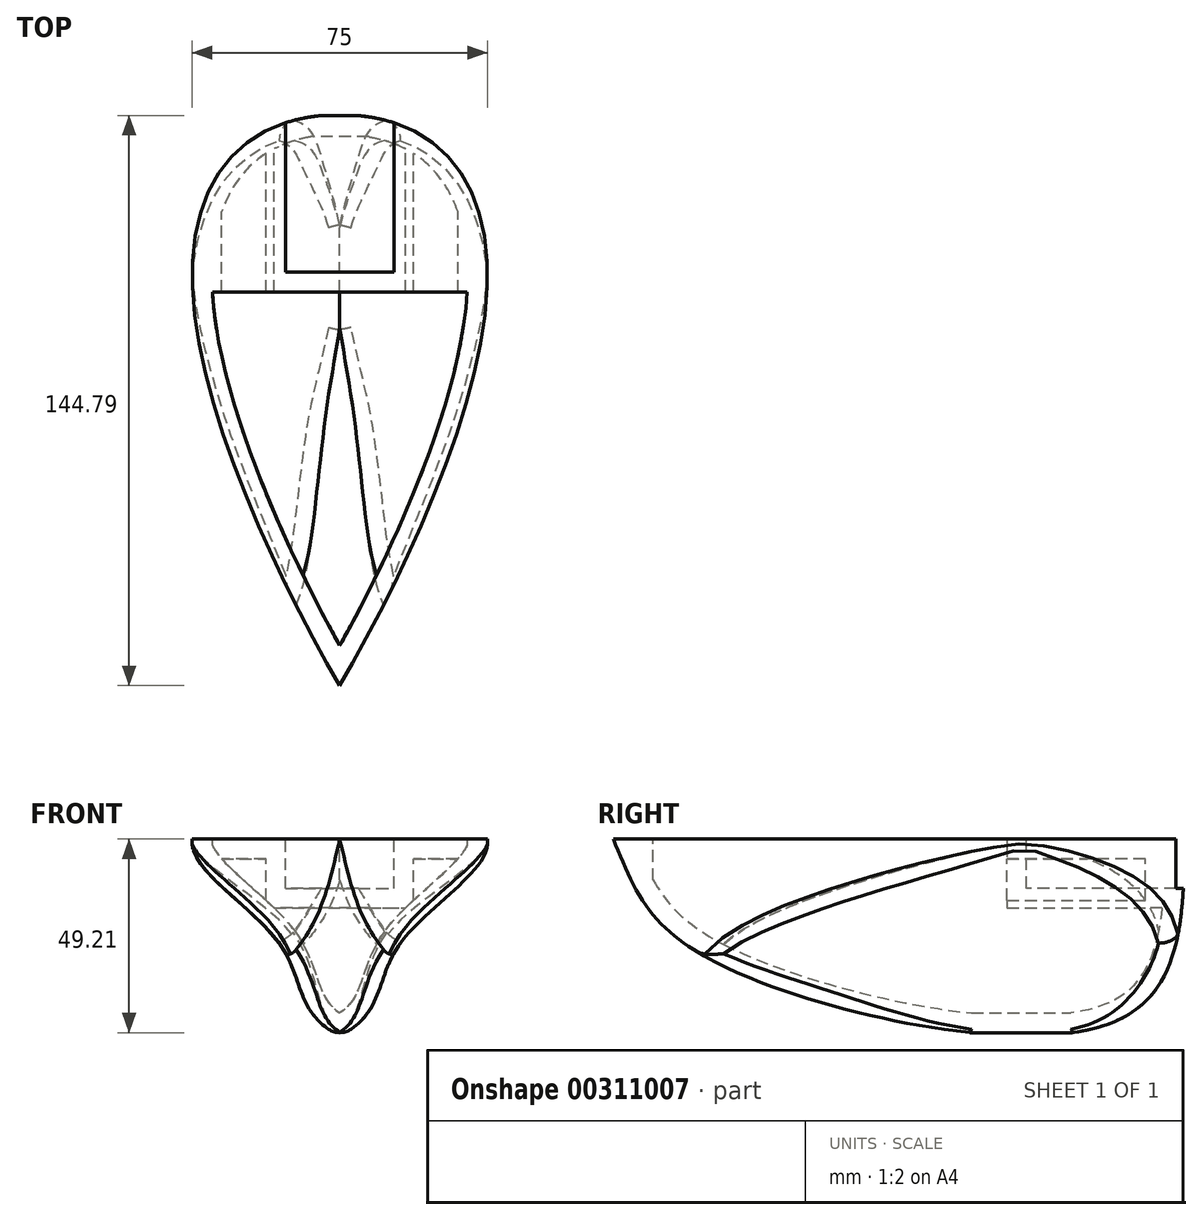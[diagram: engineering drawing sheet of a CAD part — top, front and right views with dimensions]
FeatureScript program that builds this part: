
annotation { "Feature Type Name" : "Feature", "Feature Type Description" : "" }
export const myFeature = defineFeature(function(context is Context, id is Id, definition is map)
    precondition{}
    {
        {
            var Q0;
            Q0=qCreatedBy(makeId("Front.planeOp"),FACE);
            var sketch = newSketch(context, id + "F0", { "sketchPlane" : qUnion([Q0])});
            skFitSpline(sketch, "E0", {"points": [v(-37.5, 0) * mm, v(-15, -27) * mm, v(0, -50) * mm], "startDerivative": vector(-7.17, -44.73) * mm, "endDerivative": vector(72.64, -36.53) * mm});
            skLineSegment(sketch, "E1", {"start": v(0, 0) * mm, "end": v(0, -50) * mm, "construction": true});
            skFitSpline(sketch, "E2.MirrorCS", {"points": [v(37.5, 0) * mm, v(15, -27) * mm, v(0, -50) * mm], "startDerivative": vector(7.17, -44.73) * mm, "endDerivative": vector(-72.64, -36.53) * mm});
            skLineSegment(sketch, "E3", {"start": v(-37.5, 0) * mm, "end": v(37.5, 0) * mm});
            skSolve(sketch);
        }
        {
            var Q0;
            Q0 = qSketchRegion(id + "F0", true);
            extrude(context, id + "F1", {"entities" : qUnion([Q0]), "depth" : 145 * mm});
        }
        {
            var Q0;
            Q0=qCreatedBy(makeId("Right.planeOp"),FACE);
            var sketch = newSketch(context, id + "F2", { "sketchPlane" : qUnion([Q0])});
            skFitSpline(sketch, "E4", {"points": [v(-145, 0) * mm, v(-137.3, -16.05) * mm, v(-112.75, -34.3) * mm, v(-15.25, -45.26) * mm, v(0, 0) * mm], "startDerivative": vector(48.1, -120.7) * mm, "endDerivative": vector(-0.52, 209.34) * mm});
            skLineSegment(sketch, "E5", {"start": v(-145, 0) * mm, "end": v(0, 0) * mm});
            skSolve(sketch);
        }
        {
            var Q0;
            Q0 = qSketchRegion(id + "F2", true);
            extrude(context, id + "F3", {"entities" : qUnion([Q0]), "operationType" : NewBodyOperationType.INTERSECT, "depth" : 48 * mm, "hasSecondDirection" : true, "secondDirectionOppositeDirection" : true, "secondDirectionDepth" : 44 * mm});
        }
        {
            var Q0;
            Q0=qCreatedBy(makeId("Top.planeOp"),FACE);
            var sketch = newSketch(context, id + "F4", { "sketchPlane" : qUnion([Q0])});
            skFitSpline(sketch, "E6", {"points": [v(0, 0) * mm, v(-37.4, -37) * mm, v(0, -145) * mm], "startDerivative": vector(-174.54, 0) * mm, "endDerivative": vector(81.14, -138.92) * mm});
            skLineSegment(sketch, "E7", {"start": v(0, 0) * mm, "end": v(0, -145) * mm, "construction": true});
            skFitSpline(sketch, "E8.MirrorCS", {"points": [v(0, 0) * mm, v(37.4, -37) * mm, v(0, -145) * mm], "startDerivative": vector(174.54, 0) * mm, "endDerivative": vector(-81.14, -138.92) * mm});
            skSolve(sketch);
        }
        {
            var Q0;
            Q0 = qSketchRegion(id + "F4", true);
            extrude(context, id + "F5", {"entities" : qUnion([Q0]), "operationType" : NewBodyOperationType.INTERSECT, "oppositeDirection" : true, "depth" : 54 * mm});
        }
        {
            var Q0;
            Q0=makeQuery(id+"F1.opExtrude","SWEPT_FACE",FACE,{"disambiguationData":[OSD([sQuery(id+"F0.wireOp",EDGE,"E3")])]});
            var sketch = newSketch(context, id + "F6", { "sketchPlane" : qUnion([Q0])});
            skLineSegment(sketch, "E9.bottom", {"start": v(-13.75, 0) * mm, "end": v(13.75, 0) * mm});
            skLineSegment(sketch, "E9.top", {"start": v(-13.75, -40) * mm, "end": v(13.75, -40) * mm});
            skLineSegment(sketch, "E9.left", {"start": v(-13.75, 0) * mm, "end": v(-13.75, -40) * mm});
            skLineSegment(sketch, "E9.right", {"start": v(13.75, 0) * mm, "end": v(13.75, -40) * mm});
            skPoint(sketch, "E9.middle", {"position": v(0, -20) * mm});
            skFitSpline(sketch, "E10.0", {"points": [v(0, 0) * mm, v(-23.52, 0) * mm, v(-54.86, -36.99) * mm, v(-16.11, -117.41) * mm, v(0, -145) * mm]});
            skFitSpline(sketch, "E11.0", {"points": [v(0, 0) * mm, v(23.52, 0) * mm, v(54.86, -36.99) * mm, v(16.11, -117.41) * mm, v(0, -145) * mm]});
            skSolve(sketch);
        }
        {
            var Q0;
            {var subQ1=sQuery(id+"F6.wireOp",EDGE,"E9.top");Q0=makeQuery(id+"F6.imprint","IMPRINT",FACE,{"disambiguationData":[TD([[makeQuery(id+"F6.imprint","IMPRINT",EDGE,{"derivedFrom":subQ1}),1.0]])]});}
            extrude(context, id + "F7", {"entities" : qUnion([Q0]), "operationType" : NewBodyOperationType.REMOVE, "oppositeDirection" : true, "depth" : 12.5 * mm});
        }
        {
            var Q0;
            Q0=makeQuery(id+"F1.opExtrude","SWEPT_FACE",FACE,{"disambiguationData":[OSD([sQuery(id+"F0.wireOp",EDGE,"E3")])]});
            var Q1;
            Q1=makeQuery(id+"F1.opExtrude","SWEPT_BODY",BODY,{"disambiguationData":[OSD([sQuery(id+"F0.wireOp",EDGE,"E0"),sQuery(id+"F0.wireOp",EDGE,"E2.MirrorCS"),sQuery(id+"F0.wireOp",EDGE,"E3")])]});
            shell(context, id + "F8", {"entities" : qUnion([Q0]), "parts" : qUnion([Q1]), "thickness" : 5 * mm});
        }
        {
            var Q0;
            Q0=makeQuery(id+"F1.opExtrude","SWEPT_FACE",FACE,{"disambiguationData":[OSD([sQuery(id+"F0.wireOp",EDGE,"E3")])]});
            var sketch = newSketch(context, id + "F9", { "sketchPlane" : qUnion([Q0])});
            skLineSegment(sketch, "E12", {"start": v(-37.38, -45) * mm, "end": v(37.38, -45) * mm});
            skPoint(sketch, "E13", {"position": v(-32.37, -45) * mm});
            skPoint(sketch, "E14", {"position": v(-4.48, -45) * mm});
            skSolve(sketch);
        }
        {
            var Q0;
            {var subQ0=sQuery(id+"F6.wireOp",EDGE,"E9.left");var subQ1=makeQuery(id+"F8.opShell","OFFSET_EDGE",EDGE,{"disambiguationData":[OSD([subQ0]),TDD([makeQuery(id+"F7.boolean.opBoolean","COPY",EDGE,{"derivedFrom":makeQuery(id+"F7.opExtrude","CAP_EDGE",EDGE,{"disambiguationData":[OSD([subQ0])],"isStart":true})})])]});Q0=makeQuery(id+"F9.imprint","IMPRINT",FACE,{"disambiguationData":[TD([[makeQuery(id+"F9.imprint","IMPRINT",EDGE,{"derivedFrom":subQ1}),-1.0]])]});}
            var Q1;
            {var subQ2=sQuery(id+"F6.wireOp",EDGE,"E9.right");var subQ3=makeQuery(id+"F8.opShell","OFFSET_EDGE",EDGE,{"disambiguationData":[OSD([subQ2]),TDD([makeQuery(id+"F7.boolean.opBoolean","COPY",EDGE,{"derivedFrom":makeQuery(id+"F7.opExtrude","CAP_EDGE",EDGE,{"disambiguationData":[OSD([subQ2])],"isStart":true})})])]});Q1=makeQuery(id+"F9.imprint","IMPRINT",FACE,{"disambiguationData":[TD([[makeQuery(id+"F9.imprint","IMPRINT",EDGE,{"derivedFrom":subQ3}),1.0]])]});}
            extrude(context, id + "F10", {"entities" : qUnion([Q0, Q1]), "operationType" : NewBodyOperationType.ADD, "oppositeDirection" : true, "depth" : 5 * mm});
        }
        {
            var Q0;
            Q0=makeQuery(id+"F1.opExtrude","SWEPT_FACE",FACE,{"disambiguationData":[OSD([sQuery(id+"F0.wireOp",EDGE,"E2.MirrorCS")])]});
            var Q1;
            Q1=makeQuery(id+"F1.opExtrude","SWEPT_FACE",FACE,{"disambiguationData":[OSD([sQuery(id+"F0.wireOp",EDGE,"E0")])]});
            var Q2;
            Q2=makeQuery(id+"F5.boolean.opBoolean","INTERSECT",EDGE,{"disambiguationData":[OD(1.0)],"derivedFrom":[makeQuery(id+"F3.boolean.opBoolean","COPY",FACE,{"derivedFrom":makeQuery(id+"F3.boolean.toolComplement.opBoolean","COPY",FACE,{"derivedFrom":makeQuery(id+"F3.opExtrude","SWEPT_FACE",FACE,{"disambiguationData":[OSD([sQuery(id+"F2.wireOp",EDGE,"E4")])]})})}),makeQuery(id+"F5.boolean.toolComplement.opBoolean","COPY",FACE,{"derivedFrom":makeQuery(id+"F5.opExtrude","SWEPT_FACE",FACE,{"disambiguationData":[OSD([sQuery(id+"F4.wireOp",EDGE,"E6")])]})})]});
            var Q3;
            Q3=makeQuery(id+"F5.boolean.opBoolean","INTERSECT",EDGE,{"disambiguationData":[OD(1.0)],"derivedFrom":[makeQuery(id+"F3.boolean.opBoolean","COPY",FACE,{"derivedFrom":makeQuery(id+"F3.boolean.toolComplement.opBoolean","COPY",FACE,{"derivedFrom":makeQuery(id+"F3.opExtrude","SWEPT_FACE",FACE,{"disambiguationData":[OSD([sQuery(id+"F2.wireOp",EDGE,"E4")])]})})}),makeQuery(id+"F5.boolean.toolComplement.opBoolean","COPY",FACE,{"derivedFrom":makeQuery(id+"F5.opExtrude","SWEPT_FACE",FACE,{"disambiguationData":[OSD([sQuery(id+"F4.wireOp",EDGE,"E8.MirrorCS")])]})})]});
            fillet(context, id + "F11", {"entities" : qUnion([Q0, Q1, Q2, Q3]), "radius" : 5 * mm, "tangentPropagation" : true, "allowEdgeOverflow" : false});
        }
    });
